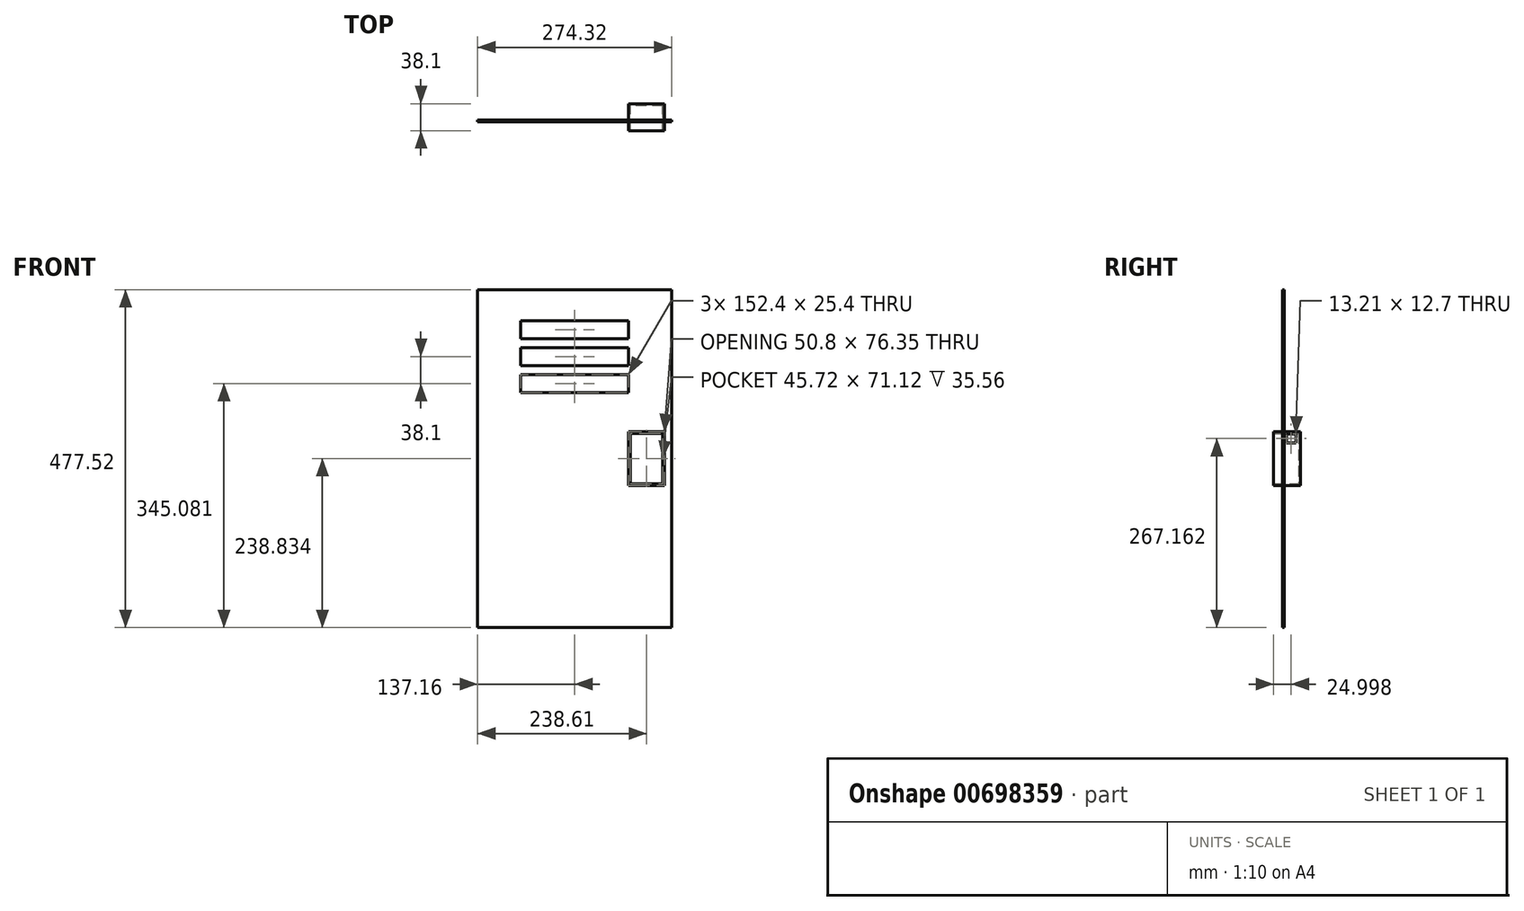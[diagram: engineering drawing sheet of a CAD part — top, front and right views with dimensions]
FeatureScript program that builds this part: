
annotation { "Feature Type Name" : "Feature", "Feature Type Description" : "" }
export const myFeature = defineFeature(function(context is Context, id is Id, definition is map)
    precondition{}
    {
        {
            var Q0;
            Q0=qCreatedBy(makeId("Front.planeOp"),FACE);
            var sketch = newSketch(context, id + "F0", { "sketchPlane" : qUnion([Q0])});
            skLineSegment(sketch, "E0.bottom", {"start": v(-137.16, 238.76) * mm, "end": v(137.16, 238.76) * mm});
            skLineSegment(sketch, "E0.top", {"start": v(-137.16, -238.76) * mm, "end": v(137.16, -238.76) * mm});
            skLineSegment(sketch, "E0.left", {"start": v(-137.16, 238.76) * mm, "end": v(-137.16, -238.76) * mm});
            skLineSegment(sketch, "E0.right", {"start": v(137.16, 238.76) * mm, "end": v(137.16, -238.76) * mm});
            skPoint(sketch, "E0.middle", {"position": v(0, 0) * mm});
            skSolve(sketch);
        }
        {
            var Q0;
            Q0 = qSketchRegion(id + "F0", true);
            extrude(context, id + "F1", {"entities" : qUnion([Q0]), "depth" : 2.54 * mm, "offsetDistance" : 25.4 * mm});
        }
        {
            var Q0;
            Q0=makeQuery(id+"F1.opExtrude","CAP_FACE",FACE,{"disambiguationData":[OSD([sQuery(id+"F0.wireOp",EDGE,"E0.bottom"),sQuery(id+"F0.wireOp",EDGE,"E0.top"),sQuery(id+"F0.wireOp",EDGE,"E0.left"),sQuery(id+"F0.wireOp",EDGE,"E0.right")])],"isStart":false});
            var sketch = newSketch(context, id + "F2", { "sketchPlane" : qUnion([Q0])});
            skLineSegment(sketch, "E1.bottom", {"start": v(76.2, 169.82) * mm, "end": v(-76.2, 169.82) * mm});
            skLineSegment(sketch, "E1.top", {"start": v(76.2, 195.22) * mm, "end": v(-76.2, 195.22) * mm});
            skLineSegment(sketch, "E1.left", {"start": v(76.2, 169.82) * mm, "end": v(76.2, 195.22) * mm});
            skLineSegment(sketch, "E1.right", {"start": v(-76.2, 169.82) * mm, "end": v(-76.2, 195.22) * mm});
            skPoint(sketch, "E1.middle", {"position": v(0, 182.52) * mm});
            skSolve(sketch);
        }
        {
            var Q0;
            Q0=makeQuery(id+"F2.imprint","IMPRINT",FACE,{"disambiguationData":[TD([[makeQuery(id+"F2.imprint","IMPRINT",EDGE,{"derivedFrom":sQuery(id+"F2.wireOp",EDGE,"E1.bottom")}),1.0]])]});
            var sketch = newSketch(context, id + "F3", { "sketchPlane" : qUnion([Q0])});
            skLineSegment(sketch, "E2.bottom", {"start": v(76.2, 131.72) * mm, "end": v(-76.2, 131.72) * mm});
            skLineSegment(sketch, "E2.top", {"start": v(76.2, 157.12) * mm, "end": v(-76.2, 157.12) * mm});
            skLineSegment(sketch, "E2.left", {"start": v(76.2, 131.72) * mm, "end": v(76.2, 157.12) * mm});
            skLineSegment(sketch, "E2.right", {"start": v(-76.2, 131.72) * mm, "end": v(-76.2, 157.12) * mm});
            skPoint(sketch, "E2.middle", {"position": v(0, 144.42) * mm});
            skSolve(sketch);
        }
        {
            var Q0;
            Q0=makeQuery(id+"F2.imprint","IMPRINT",FACE,{"disambiguationData":[TD([[makeQuery(id+"F2.imprint","IMPRINT",EDGE,{"derivedFrom":sQuery(id+"F2.wireOp",EDGE,"E1.bottom")}),1.0]])]});
            var sketch = newSketch(context, id + "F4", { "sketchPlane" : qUnion([Q0])});
            skLineSegment(sketch, "E3.bottom", {"start": v(76.2, 93.62) * mm, "end": v(-76.2, 93.62) * mm});
            skLineSegment(sketch, "E3.top", {"start": v(76.2, 119.02) * mm, "end": v(-76.2, 119.02) * mm});
            skLineSegment(sketch, "E3.left", {"start": v(76.2, 93.62) * mm, "end": v(76.2, 119.02) * mm});
            skLineSegment(sketch, "E3.right", {"start": v(-76.2, 93.62) * mm, "end": v(-76.2, 119.02) * mm});
            skPoint(sketch, "E3.middle", {"position": v(0, 106.32) * mm});
            skSolve(sketch);
        }
        {
            var Q0;
            Q0=makeQuery(id+"F2.imprint","IMPRINT",FACE,{"disambiguationData":[TD([[makeQuery(id+"F2.imprint","IMPRINT",EDGE,{"derivedFrom":sQuery(id+"F2.wireOp",EDGE,"E1.bottom")}),-1.0]])]});
            var Q1;
            Q1=makeQuery(id+"F3.imprint","IMPRINT",FACE,{"disambiguationData":[TD([[makeQuery(id+"F3.imprint","IMPRINT",EDGE,{"derivedFrom":sQuery(id+"F3.wireOp",EDGE,"E2.bottom")}),-1.0]])]});
            var Q2;
            Q2=makeQuery(id+"F4.imprint","IMPRINT",FACE,{"disambiguationData":[TD([[makeQuery(id+"F4.imprint","IMPRINT",EDGE,{"derivedFrom":sQuery(id+"F4.wireOp",EDGE,"E3.bottom")}),-1.0]])]});
            extrude(context, id + "F5", {"entities" : qUnion([Q0, Q1, Q2]), "operationType" : NewBodyOperationType.REMOVE, "oppositeDirection" : true, "depth" : 25.4 * mm, "offsetDistance" : 25.4 * mm});
        }
        {
            var Q0;
            Q0=makeQuery(id+"F1.opExtrude","CAP_FACE",FACE,{"disambiguationData":[OSD([sQuery(id+"F0.wireOp",EDGE,"E0.bottom"),sQuery(id+"F0.wireOp",EDGE,"E0.top"),sQuery(id+"F0.wireOp",EDGE,"E0.left"),sQuery(id+"F0.wireOp",EDGE,"E0.right")])],"isStart":false});
            var sketch = newSketch(context, id + "F6", { "sketchPlane" : qUnion([Q0])});
            skLineSegment(sketch, "E4.bottom", {"start": v(124.46, -38.1) * mm, "end": v(78.74, -38.1) * mm});
            skLineSegment(sketch, "E4.top", {"start": v(124.46, 38.1) * mm, "end": v(78.74, 38.1) * mm});
            skLineSegment(sketch, "E4.left", {"start": v(124.46, -38.1) * mm, "end": v(124.46, 38.1) * mm});
            skLineSegment(sketch, "E4.right", {"start": v(78.74, -38.1) * mm, "end": v(78.74, 38.1) * mm});
            skPoint(sketch, "E4.middle", {"position": v(101.6, 0) * mm});
            skSolve(sketch);
        }
        {
            var Q0;
            Q0 = qSketchRegion(id + "F6", true);
            extrude(context, id + "F7", {"entities" : qUnion([Q0]), "operationType" : NewBodyOperationType.REMOVE, "oppositeDirection" : true, "depth" : 25.4 * mm, "offsetDistance" : 25.4 * mm});
        }
        {
            var Q0;
            Q0=makeQuery(id+"F1.opExtrude","CAP_FACE",FACE,{"disambiguationData":[OSD([sQuery(id+"F0.wireOp",EDGE,"E0.bottom"),sQuery(id+"F0.wireOp",EDGE,"E0.top"),sQuery(id+"F0.wireOp",EDGE,"E0.left"),sQuery(id+"F0.wireOp",EDGE,"E0.right")])],"isStart":false});
            var sketch = newSketch(context, id + "F8", { "sketchPlane" : qUnion([Q0])});
            skPoint(sketch, "E5", {"position": v(101.6, 0) * mm});
            skPoint(sketch, "E5.positionSnap0", {"position": v(101.6, 38.1) * mm});
            skLineSegment(sketch, "E6.bottom", {"start": v(126.85, 38.25) * mm, "end": v(76.05, 38.25) * mm});
            skLineSegment(sketch, "E6.top", {"start": v(126.85, -37.95) * mm, "end": v(76.05, -37.95) * mm});
            skLineSegment(sketch, "E6.left", {"start": v(126.85, 38.25) * mm, "end": v(126.85, -37.95) * mm});
            skLineSegment(sketch, "E6.right", {"start": v(76.05, 38.25) * mm, "end": v(76.05, -37.95) * mm});
            skPoint(sketch, "E6.middle", {"position": v(101.45, 0.15) * mm});
            skSolve(sketch);
        }
        {
            var Q0;
            Q0 = qSketchRegion(id + "F8", true);
            extrude(context, id + "F9", {"entities" : qUnion([Q0]), "operationType" : NewBodyOperationType.ADD, "depth" : 12.7 * mm, "offsetDistance" : 25.4 * mm, "hasSecondDirection" : true, "secondDirectionOppositeDirection" : true, "secondDirectionDepth" : 25.4 * mm});
        }
        {
            var Q0;
            Q0=makeQuery(id+"F9.opExtrude","CAP_FACE",FACE,{"disambiguationData":[OSD([sQuery(id+"F8.wireOp",EDGE,"E6.bottom"),sQuery(id+"F8.wireOp",EDGE,"E6.top"),sQuery(id+"F8.wireOp",EDGE,"E6.left"),sQuery(id+"F8.wireOp",EDGE,"E6.right")])],"isStart":false});
            shell(context, id + "F10", {"entities" : qUnion([Q0]), "thickness" : 2.54 * mm});
        }
        {
            var Q0;
            {var subQ0=sQuery(id+"F8.wireOp",EDGE,"E6.left");Q0=makeQuery(id+"F9.boolean.opBoolean","SPLIT",FACE,{"disambiguationData":[TD([makeQuery(id+"F1.opExtrude","CAP_FACE",FACE,{"disambiguationData":[OSD([sQuery(id+"F0.wireOp",EDGE,"E0.bottom"),sQuery(id+"F0.wireOp",EDGE,"E0.top"),sQuery(id+"F0.wireOp",EDGE,"E0.left"),sQuery(id+"F0.wireOp",EDGE,"E0.right")])],"isStart":true})])],"derivedFrom":makeQuery(id+"F9.opExtrude","SWEPT_FACE",FACE,{"disambiguationData":[OSD([subQ0])]})});}
            var sketch = newSketch(context, id + "F11", { "sketchPlane" : qUnion([Q0])});
            skLineSegment(sketch, "E7.bottom", {"start": v(16.36, 34.75) * mm, "end": v(3.15, 34.75) * mm});
            skLineSegment(sketch, "E7.top", {"start": v(16.36, 22.05) * mm, "end": v(3.15, 22.05) * mm});
            skLineSegment(sketch, "E7.left", {"start": v(16.36, 34.75) * mm, "end": v(16.36, 22.05) * mm});
            skLineSegment(sketch, "E7.right", {"start": v(3.15, 34.75) * mm, "end": v(3.15, 22.05) * mm});
            skPoint(sketch, "E7.middle", {"position": v(9.76, 28.4) * mm});
            skSolve(sketch);
        }
        {
            var Q0;
            Q0=makeQuery(id+"F11.imprint","IMPRINT",FACE,{"disambiguationData":[TD([[makeQuery(id+"F11.imprint","IMPRINT",EDGE,{"derivedFrom":sQuery(id+"F11.wireOp",EDGE,"E7.bottom")}),1.0]])]});
            extrude(context, id + "F12", {"entities" : qUnion([Q0]), "operationType" : NewBodyOperationType.REMOVE, "oppositeDirection" : true, "depth" : 25.4 * mm, "offsetDistance" : 25.4 * mm});
        }
    });
